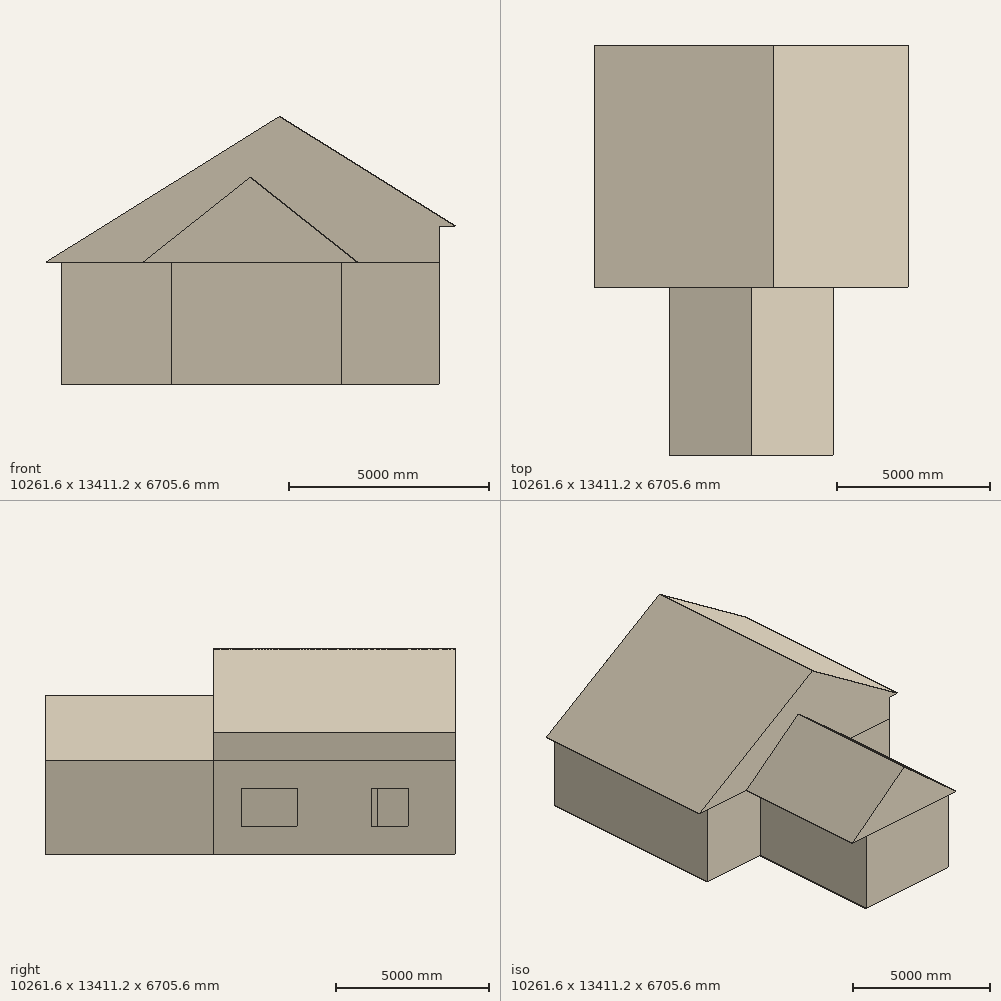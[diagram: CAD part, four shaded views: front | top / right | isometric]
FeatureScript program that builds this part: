
annotation { "Feature Type Name" : "Feature", "Feature Type Description" : "" }
export const myFeature = defineFeature(function(context is Context, id is Id, definition is map)
    precondition{}
    {
        {
            var Q0;
            Q0=qCreatedBy(makeId("Top.planeOp"),FACE);
            var sketch = newSketch(context, id + "F0", { "sketchPlane" : qUnion([Q0])});
            skLineSegment(sketch, "E0", {"start": v(-4724.4, 3962.4) * mm, "end": v(4724.4, 3962.4) * mm});
            skLineSegment(sketch, "E1", {"start": v(4724.4, 3962.4) * mm, "end": v(4724.4, -3962.4) * mm});
            skLineSegment(sketch, "E2", {"start": v(4724.4, -3962.4) * mm, "end": v(2286, -3962.4) * mm});
            skLineSegment(sketch, "E3", {"start": v(2286, -3962.4) * mm, "end": v(2286, -9448.8) * mm});
            skLineSegment(sketch, "E4", {"start": v(2286, -9448.8) * mm, "end": v(-1981.2, -9448.8) * mm});
            skLineSegment(sketch, "E5", {"start": v(-1981.2, -9448.8) * mm, "end": v(-1981.2, -3962.4) * mm});
            skLineSegment(sketch, "E6", {"start": v(-1981.2, -3962.4) * mm, "end": v(-4724.4, -3962.4) * mm});
            skLineSegment(sketch, "E7", {"start": v(-4724.4, -3962.4) * mm, "end": v(-4724.4, 3962.4) * mm});
            skSolve(sketch);
        }
        {
            var Q0;
            Q0=makeQuery(id+"F0.imprint","IMPRINT",FACE,{"disambiguationData":[TD([[makeQuery(id+"F0.imprint","IMPRINT",EDGE,{"derivedFrom":sQuery(id+"F0.wireOp",EDGE,"E0")}),-1.0]])]});
            extrude(context, id + "F1", {"entities" : qUnion([Q0]), "depth" : 3048 * mm});
        }
        {
            var Q0;
            Q0=makeQuery(id+"F1.opExtrude","CAP_FACE",FACE,{"disambiguationData":[OSD([sQuery(id+"F0.wireOp",EDGE,"E0"),sQuery(id+"F0.wireOp",EDGE,"E1"),sQuery(id+"F0.wireOp",EDGE,"E2"),sQuery(id+"F0.wireOp",EDGE,"E3"),sQuery(id+"F0.wireOp",EDGE,"E4"),sQuery(id+"F0.wireOp",EDGE,"E5"),sQuery(id+"F0.wireOp",EDGE,"E6"),sQuery(id+"F0.wireOp",EDGE,"E7")])],"isStart":false});
            var sketch = newSketch(context, id + "F2", { "sketchPlane" : qUnion([Q0])});
            skLineSegment(sketch, "E8", {"start": v(-1778, -9245.6) * mm, "end": v(2082.8, -9245.6) * mm});
            skLineSegment(sketch, "E9", {"start": v(2082.8, -9245.6) * mm, "end": v(2082.8, -4775.2) * mm});
            skLineSegment(sketch, "E10", {"start": v(2082.8, -4775.2) * mm, "end": v(1778, -4775.2) * mm});
            skLineSegment(sketch, "E11", {"start": v(1778, -4775.2) * mm, "end": v(1778, -4572) * mm});
            skLineSegment(sketch, "E12", {"start": v(1778, -4572) * mm, "end": v(2082.8, -4572) * mm});
            skLineSegment(sketch, "E13", {"start": v(2082.8, -4572) * mm, "end": v(2082.8, -3962.4) * mm});
            skLineSegment(sketch, "E14", {"start": v(2082.8, -3962.4) * mm, "end": v(152.4, -3962.4) * mm});
            skLineSegment(sketch, "E15", {"start": v(152.4, -3962.4) * mm, "end": v(152.4, -4572) * mm});
            skLineSegment(sketch, "E16", {"start": v(152.4, -4572) * mm, "end": v(254, -4572) * mm});
            skLineSegment(sketch, "E17", {"start": v(254, -4572) * mm, "end": v(254, -4775.2) * mm});
            skLineSegment(sketch, "E18", {"start": v(254, -4775.2) * mm, "end": v(-50.8, -4775.2) * mm});
            skLineSegment(sketch, "E19", {"start": v(-50.8, -4775.2) * mm, "end": v(-50.8, -3759.2) * mm});
            skLineSegment(sketch, "E20", {"start": v(-50.8, -3759.2) * mm, "end": v(4521.2, -3759.2) * mm});
            skLineSegment(sketch, "E21", {"start": v(-1778, -9245.6) * mm, "end": v(-1778, -4775.2) * mm});
            skLineSegment(sketch, "E22", {"start": v(-1778, -4775.2) * mm, "end": v(-660.4, -4775.2) * mm});
            skLineSegment(sketch, "E23", {"start": v(-660.4, -4775.2) * mm, "end": v(-660.4, -3759.2) * mm});
            skLineSegment(sketch, "E24", {"start": v(-660.4, -3759.2) * mm, "end": v(-1778, -3759.2) * mm});
            skLineSegment(sketch, "E25", {"start": v(-1778, -3759.2) * mm, "end": v(-1778, 406.4) * mm});
            skLineSegment(sketch, "E26", {"start": v(4521.2, -3759.2) * mm, "end": v(4521.2, 406.4) * mm});
            skLineSegment(sketch, "E27", {"start": v(4521.2, 406.4) * mm, "end": v(711.2, 406.4) * mm});
            skLineSegment(sketch, "E28", {"start": v(711.2, 406.4) * mm, "end": v(711.2, 609.6) * mm});
            skLineSegment(sketch, "E29", {"start": v(711.2, 609.6) * mm, "end": v(2489.2, 609.6) * mm});
            skLineSegment(sketch, "E30", {"start": v(2489.2, 609.6) * mm, "end": v(2489.2, 1219.2) * mm});
            skLineSegment(sketch, "E31", {"start": v(2489.2, 1219.2) * mm, "end": v(2692.4, 1219.2) * mm});
            skLineSegment(sketch, "E32", {"start": v(2692.4, 1219.2) * mm, "end": v(2692.4, 609.6) * mm});
            skLineSegment(sketch, "E33", {"start": v(2692.4, 609.6) * mm, "end": v(4521.2, 609.6) * mm});
            skLineSegment(sketch, "E34", {"start": v(4521.2, 609.6) * mm, "end": v(4521.2, 3759.2) * mm});
            skLineSegment(sketch, "E35", {"start": v(4521.2, 3759.2) * mm, "end": v(2692.4, 3759.2) * mm});
            skLineSegment(sketch, "E36", {"start": v(2692.4, 3759.2) * mm, "end": v(2692.4, 3149.6) * mm});
            skLineSegment(sketch, "E37", {"start": v(2692.4, 3149.6) * mm, "end": v(2489.2, 3149.6) * mm});
            skLineSegment(sketch, "E38", {"start": v(2489.2, 3149.6) * mm, "end": v(2489.2, 3759.2) * mm});
            skLineSegment(sketch, "E39", {"start": v(2489.2, 3759.2) * mm, "end": v(-1778, 3759.2) * mm});
            skLineSegment(sketch, "E40", {"start": v(-4521.2, 3759.2) * mm, "end": v(-4521.2, 1625.6) * mm});
            skLineSegment(sketch, "E41", {"start": v(-4521.2, 1625.6) * mm, "end": v(-1981.2, 1625.6) * mm});
            skLineSegment(sketch, "E42", {"start": v(-1981.2, 1625.6) * mm, "end": v(-1981.2, 2540) * mm});
            skLineSegment(sketch, "E43", {"start": v(-1981.2, 2540) * mm, "end": v(-1778, 2540) * mm});
            skLineSegment(sketch, "E44", {"start": v(-1778, 2540) * mm, "end": v(-1778, 1422.4) * mm});
            skLineSegment(sketch, "E45", {"start": v(-1778, 1422.4) * mm, "end": v(-4521.2, 1422.4) * mm});
            skLineSegment(sketch, "E46", {"start": v(-4521.2, 1422.4) * mm, "end": v(-4521.2, -3759.2) * mm});
            skLineSegment(sketch, "E47", {"start": v(-4521.2, -3759.2) * mm, "end": v(-1981.2, -3759.2) * mm});
            skLineSegment(sketch, "E48", {"start": v(-1981.2, -3759.2) * mm, "end": v(-1981.2, 609.6) * mm});
            skLineSegment(sketch, "E49", {"start": v(-1981.2, 609.6) * mm, "end": v(-50.8, 609.6) * mm});
            skLineSegment(sketch, "E50", {"start": v(-50.8, 609.6) * mm, "end": v(-50.8, 406.4) * mm});
            skLineSegment(sketch, "E51", {"start": v(-50.8, 406.4) * mm, "end": v(-660.4, 406.4) * mm});
            skLineSegment(sketch, "E52", {"start": v(-660.4, 406.4) * mm, "end": v(-660.4, -3149.6) * mm});
            skLineSegment(sketch, "E53", {"start": v(-660.4, -3149.6) * mm, "end": v(-863.6, -3149.6) * mm});
            skLineSegment(sketch, "E54", {"start": v(-863.6, -3149.6) * mm, "end": v(-863.6, 406.4) * mm});
            skLineSegment(sketch, "E55", {"start": v(-863.6, 406.4) * mm, "end": v(-1778, 406.4) * mm});
            skLineSegment(sketch, "E56", {"start": v(-1778, 3759.2) * mm, "end": v(-1778, 3149.6) * mm});
            skLineSegment(sketch, "E57", {"start": v(-1778, 3149.6) * mm, "end": v(-1981.2, 3149.6) * mm});
            skLineSegment(sketch, "E58", {"start": v(-1981.2, 3149.6) * mm, "end": v(-1981.2, 3759.2) * mm});
            skLineSegment(sketch, "E59", {"start": v(-1981.2, 3759.2) * mm, "end": v(-4521.2, 3759.2) * mm});
            skSolve(sketch);
        }
        {
            var Q0;
            Q0 = qSketchRegion(id + "F2", true);
            extrude(context, id + "F3", {"entities" : qUnion([Q0]), "operationType" : NewBodyOperationType.REMOVE, "oppositeDirection" : true, "depth" : 2743.2 * mm - 203.2 * mm});
        }
        {
            var Q0;
            Q0=makeQuery(id+"F1.opExtrude","CAP_FACE",FACE,{"disambiguationData":[OSD([sQuery(id+"F0.wireOp",EDGE,"E0"),sQuery(id+"F0.wireOp",EDGE,"E1"),sQuery(id+"F0.wireOp",EDGE,"E2"),sQuery(id+"F0.wireOp",EDGE,"E3"),sQuery(id+"F0.wireOp",EDGE,"E4"),sQuery(id+"F0.wireOp",EDGE,"E5"),sQuery(id+"F0.wireOp",EDGE,"E6"),sQuery(id+"F0.wireOp",EDGE,"E7")])],"isStart":true});
            var sketch = newSketch(context, id + "F4", { "sketchPlane" : qUnion([Q0])});
            skLineSegment(sketch, "E60.bottom", {"start": v(-1981.2, -3962.4) * mm, "end": v(2286, -3962.4) * mm});
            skLineSegment(sketch, "E60.top", {"start": v(-1981.2, 3962.4) * mm, "end": v(2286, 3962.4) * mm});
            skLineSegment(sketch, "E60.left", {"start": v(-1981.2, -3962.4) * mm, "end": v(-1981.2, 3962.4) * mm});
            skLineSegment(sketch, "E60.right", {"start": v(2286, -3962.4) * mm, "end": v(2286, 3962.4) * mm});
            skLineSegment(sketch, "E61.bottom", {"start": v(-1778, -3759.2) * mm, "end": v(2082.8, -3759.2) * mm});
            skLineSegment(sketch, "E61.top", {"start": v(-1778, 3759.2) * mm, "end": v(2082.8, 3759.2) * mm});
            skLineSegment(sketch, "E61.left", {"start": v(-1778, -3759.2) * mm, "end": v(-1778, 3759.2) * mm});
            skLineSegment(sketch, "E61.right", {"start": v(2082.8, -3759.2) * mm, "end": v(2082.8, 3759.2) * mm});
            skSolve(sketch);
        }
        {
            var Q0;
            Q0=makeQuery(id+"F1.opExtrude","SWEPT_FACE",FACE,{"disambiguationData":[OSD([sQuery(id+"F0.wireOp",EDGE,"E1")])]});
            var sketch = newSketch(context, id + "F5", { "sketchPlane" : qUnion([Q0])});
            skLineSegment(sketch, "E62.bottom", {"start": v(-3048, 2133.6) * mm, "end": v(-1219.2, 2133.6) * mm});
            skLineSegment(sketch, "E62.top", {"start": v(-3048, 914.4) * mm, "end": v(-1219.2, 914.4) * mm});
            skLineSegment(sketch, "E62.left", {"start": v(-3048, 2133.6) * mm, "end": v(-3048, 914.4) * mm});
            skLineSegment(sketch, "E62.right", {"start": v(-1219.2, 2133.6) * mm, "end": v(-1219.2, 914.4) * mm});
            skLineSegment(sketch, "E63.bottom", {"start": v(1219.2, 2133.6) * mm, "end": v(2438.4, 2133.6) * mm});
            skLineSegment(sketch, "E63.top", {"start": v(1219.2, 914.4) * mm, "end": v(2438.4, 914.4) * mm});
            skLineSegment(sketch, "E63.left", {"start": v(1219.2, 2133.6) * mm, "end": v(1219.2, 914.4) * mm});
            skLineSegment(sketch, "E63.right", {"start": v(2438.4, 2133.6) * mm, "end": v(2438.4, 914.4) * mm});
            skSolve(sketch);
        }
        {
            var Q0;
            Q0 = qSketchRegion(id + "F5", true);
            extrude(context, id + "F6", {"entities" : qUnion([Q0]), "operationType" : NewBodyOperationType.REMOVE, "oppositeDirection" : true, "depth" : 304.8 * mm});
        }
        {
            var Q0;
            Q0=makeQuery(id+"F1.opExtrude","SWEPT_FACE",FACE,{"disambiguationData":[OSD([sQuery(id+"F0.wireOp",EDGE,"E4")])]});
            var sketch = newSketch(context, id + "F7", { "sketchPlane" : qUnion([Q0])});
            skLineSegment(sketch, "E64", {"start": v(-2692.4, 3048) * mm, "end": v(0, 5181.6) * mm});
            skLineSegment(sketch, "E65", {"start": v(0, 5181.6) * mm, "end": v(2692.4, 3048) * mm});
            skLineSegment(sketch, "E66", {"start": v(2692.4, 3048) * mm, "end": v(-2692.4, 3048) * mm});
            skLineSegment(sketch, "E67", {"start": v(152.4, 0) * mm, "end": v(152.4, 3048) * mm, "construction": true});
            skSolve(sketch);
        }
        {
            var Q0;
            {var subQ5=sQuery(id+"F7.wireOp",EDGE,"E64");Q0=makeQuery(id+"F7.imprint","IMPRINT",FACE,{"disambiguationData":[TD([[makeQuery(id+"F7.imprint","IMPRINT",EDGE,{"derivedFrom":subQ5}),-1.0]])]});}
            var Q1;
            Q1=makeQuery(id+"F1.opExtrude","SWEPT_FACE",FACE,{"disambiguationData":[OSD([sQuery(id+"F0.wireOp",EDGE,"E2")])]});
            var Q2;
            Q2=makeQuery(id+"F1.opExtrude","CAP_VERTEX",VERTEX,{"disambiguationData":[OSD([sQuery(id+"F0.wireOp",EDGE,"E2"),sQuery(id+"F0.wireOp",EDGE,"E3")])],"isStart":false});
            extrude(context, id + "F8", {"entities" : qUnion([Q0]), "oppositeDirection" : true, "depth" : 5486.4 * mm, "endBoundEntityFace" : qUnion([Q1]), "endBoundEntityVertex" : qUnion([Q2]), "offsetDistance" : 25.4 * mm});
        }
        {
            var Q0;
            Q0=makeQuery(id+"FGIZ5U2coVkWDJl_1.boolean.opBoolean","MERGE",FACE,{"derivedFrom":[makeQuery(id+"F1.opExtrude","SWEPT_FACE",FACE,{"disambiguationData":[OSD([sQuery(id+"F0.wireOp",EDGE,"E0")])]}),makeQuery(id+"FGIZ5U2coVkWDJl_1.opExtrude","SWEPT_FACE",FACE,{"disambiguationData":[OSD([sQuery(id+"F4.wireOp",EDGE,"E60.bottom")])]})]});
            var sketch = newSketch(context, id + "F9", { "sketchPlane" : qUnion([Q0])});
            skLineSegment(sketch, "E68", {"start": v(-4724.4, 3048) * mm, "end": v(-4724.4, 3962.4) * mm});
            skLineSegment(sketch, "E69", {"start": v(-4724.4, 3962.4) * mm, "end": v(-5130.8, 3962.4) * mm});
            skLineSegment(sketch, "E70", {"start": v(-5130.8, 3962.4) * mm, "end": v(-732.97, 6705.6) * mm});
            skLineSegment(sketch, "E71", {"start": v(-732.97, 6705.6) * mm, "end": v(5130.8, 3048) * mm});
            skLineSegment(sketch, "E72", {"start": v(5130.8, 3048) * mm, "end": v(4724.4, 3048) * mm});
            skLineSegment(sketch, "E73", {"start": v(-732.97, 6705.6) * mm, "end": v(-732.97, 8900.86) * mm, "construction": true});
            skSolve(sketch);
        }
        {
            var Q0;
            Q0=makeQuery(id+"F9.imprint","IMPRINT",FACE,{"disambiguationData":[TD([[makeQuery(id+"F9.imprint","IMPRINT",EDGE,{"derivedFrom":sQuery(id+"F9.wireOp",EDGE,"E68")}),-1.0]])]});
            var Q1;
            Q1=makeQuery(id+"F8.opExtrude","SWEPT_BODY",BODY,{"disambiguationData":[OSD([sQuery(id+"F7.wireOp",EDGE,"E64"),sQuery(id+"F7.wireOp",EDGE,"E65"),sQuery(id+"F7.wireOp",EDGE,"E66")])]});
            extrude(context, id + "F10", {"entities" : qUnion([Q0]), "oppositeDirection" : true, "depth" : 7924.8 * mm, "endBoundEntityBody" : qUnion([Q1]), "offsetDistance" : 25.4 * mm});
        }
    });
